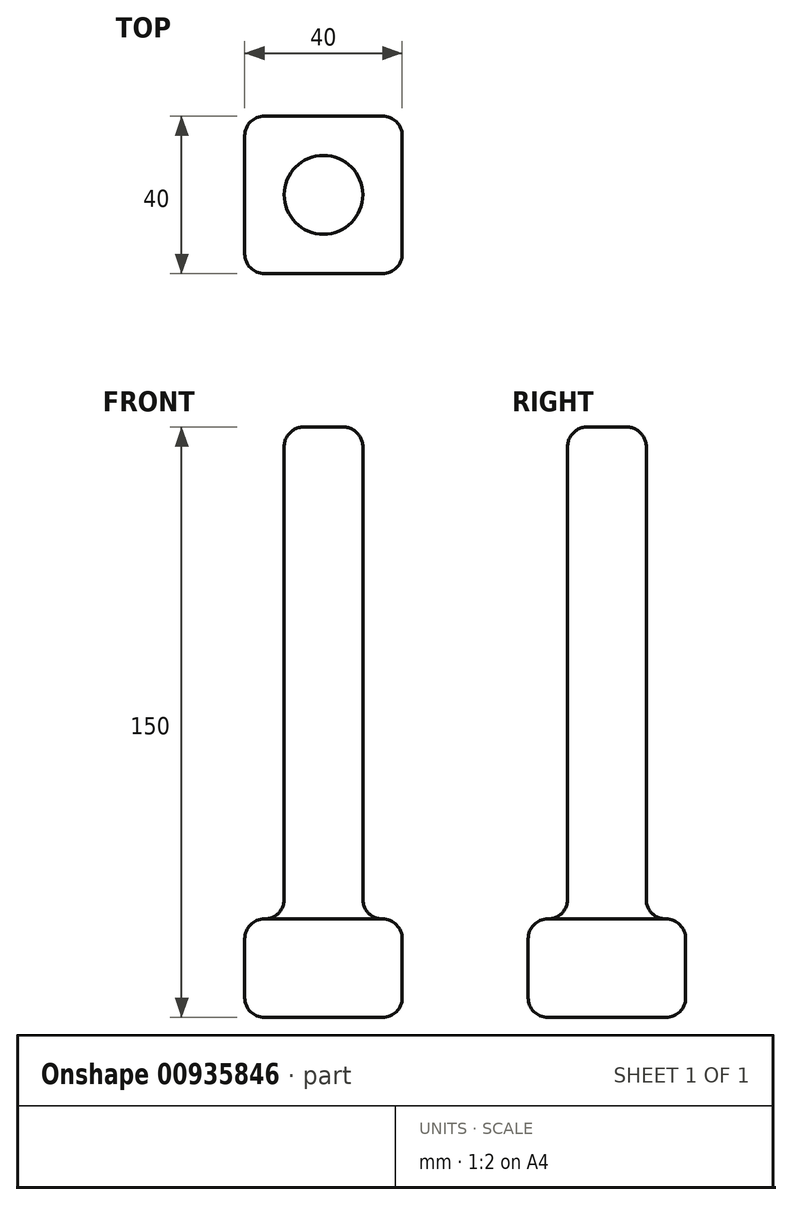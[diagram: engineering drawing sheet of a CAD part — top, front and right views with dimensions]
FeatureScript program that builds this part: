
annotation { "Feature Type Name" : "Feature", "Feature Type Description" : "" }
export const myFeature = defineFeature(function(context is Context, id is Id, definition is map)
    precondition{}
    {
        {
            var Q0;
            Q0=qCreatedBy(makeId("Top.planeOp"),FACE);
            var sketch = newSketch(context, id + "F0", { "sketchPlane" : qUnion([Q0])});
            skLineSegment(sketch, "E0.bottom", {"start": v(20, 20) * mm, "end": v(-20, 20) * mm});
            skLineSegment(sketch, "E0.top", {"start": v(20, -20) * mm, "end": v(-20, -20) * mm});
            skLineSegment(sketch, "E0.left", {"start": v(20, 20) * mm, "end": v(20, -20) * mm});
            skLineSegment(sketch, "E0.right", {"start": v(-20, 20) * mm, "end": v(-20, -20) * mm});
            skPoint(sketch, "E0.middle", {"position": v(0, 0) * mm});
            skCircle(sketch, "E1", {"center": v(0, 0) * mm, "radius": 10 * mm});
            skSolve(sketch);
        }
        {
            var Q0;
            Q0=makeQuery(id+"F0.imprint","IMPRINT",FACE,{"disambiguationData":[TD([[makeQuery(id+"F0.imprint","IMPRINT",EDGE,{"derivedFrom":sQuery(id+"F0.wireOp",EDGE,"E0.bottom")}),1.0]])]});
            extrude(context, id + "F1", {"entities" : qUnion([Q0]), "depth" : 25 * mm, "offsetDistance" : 25 * mm});
        }
        {
            var Q0;
            Q0=makeQuery(id+"F0.imprint","IMPRINT",FACE,{"disambiguationData":[TD([[makeQuery(id+"F0.imprint","IMPRINT",EDGE,{"derivedFrom":sQuery(id+"F0.wireOp",EDGE,"E1")}),1.0]])]});
            extrude(context, id + "F2", {"entities" : qUnion([Q0]), "operationType" : NewBodyOperationType.ADD, "depth" : 150 * mm, "offsetDistance" : 25 * mm});
        }
        {
            var Q0;
            {var subQ0=sQuery(id+"F0.wireOp",EDGE,"E1");Q0=makeQuery(id+"F2.boolean.opBoolean","MERGE",FACE,{"derivedFrom":[makeQuery(id+"F1.opExtrude","CAP_FACE",FACE,{"disambiguationData":[OSD([sQuery(id+"F0.wireOp",EDGE,"E0.bottom"),sQuery(id+"F0.wireOp",EDGE,"E0.top"),sQuery(id+"F0.wireOp",EDGE,"E0.left"),sQuery(id+"F0.wireOp",EDGE,"E0.right"),subQ0])],"isStart":true}),makeQuery(id+"F2.opExtrude","CAP_FACE",FACE,{"disambiguationData":[OSD([subQ0])],"isStart":true})]});}
            var Q1;
            Q1=makeQuery(id+"F1.opExtrude","SWEPT_FACE",FACE,{"disambiguationData":[OSD([sQuery(id+"F0.wireOp",EDGE,"E0.right")])]});
            var Q2;
            Q2=makeQuery(id+"F1.opExtrude","SWEPT_FACE",FACE,{"disambiguationData":[OSD([sQuery(id+"F0.wireOp",EDGE,"E0.top")])]});
            var Q3;
            Q3=makeQuery(id+"F2.opExtrude","SWEPT_FACE",FACE,{"disambiguationData":[OSD([sQuery(id+"F0.wireOp",EDGE,"E1")])]});
            var Q4;
            Q4=makeQuery(id+"F1.opExtrude","SWEPT_FACE",FACE,{"disambiguationData":[OSD([sQuery(id+"F0.wireOp",EDGE,"E0.left")])]});
            var Q5;
            Q5=makeQuery(id+"F2.opExtrude","CAP_FACE",FACE,{"disambiguationData":[OSD([sQuery(id+"F0.wireOp",EDGE,"E1")])],"isStart":false});
            var Q6;
            Q6=makeQuery(id+"F1.opExtrude","CAP_EDGE",EDGE,{"disambiguationData":[OSD([sQuery(id+"F0.wireOp",EDGE,"E0.bottom")])],"isStart":false});
            var Q7;
            Q7=makeQuery(id+"F1.opExtrude","CAP_FACE",FACE,{"disambiguationData":[OSD([sQuery(id+"F0.wireOp",EDGE,"E0.bottom"),sQuery(id+"F0.wireOp",EDGE,"E0.top"),sQuery(id+"F0.wireOp",EDGE,"E0.left"),sQuery(id+"F0.wireOp",EDGE,"E0.right"),sQuery(id+"F0.wireOp",EDGE,"E1")])],"isStart":false});
            fillet(context, id + "F3", {"entities" : qUnion([Q0, Q1, Q2, Q3, Q4, Q5, Q6, Q7]), "radius" : 5 * mm, "tangentPropagation" : true, "allowEdgeOverflow" : false});
        }
    });
